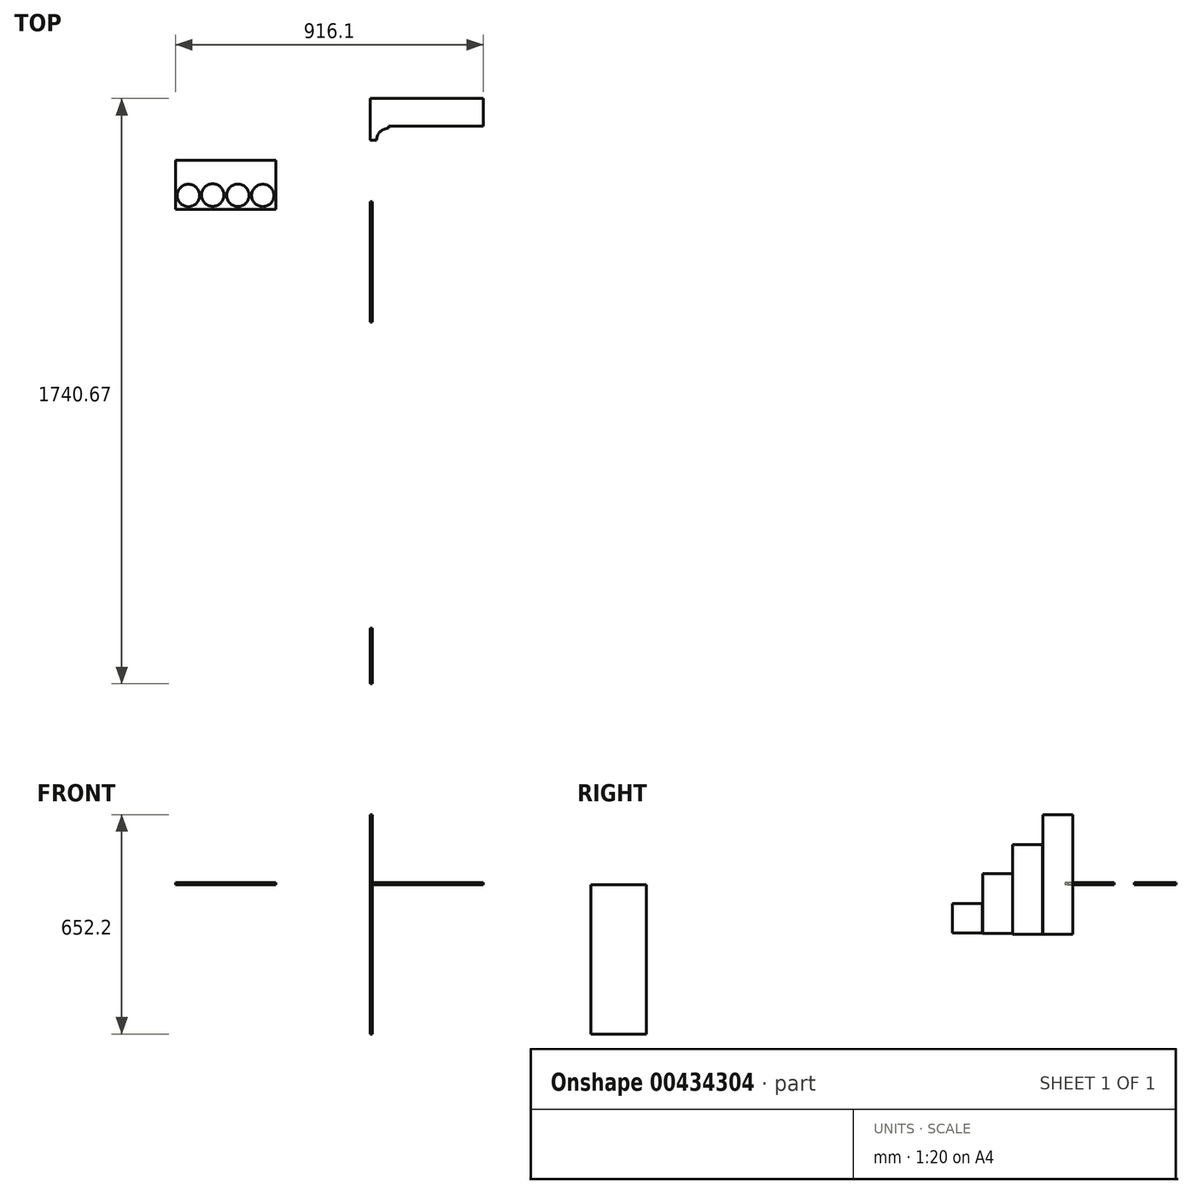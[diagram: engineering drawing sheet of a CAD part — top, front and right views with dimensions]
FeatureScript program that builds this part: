
annotation { "Feature Type Name" : "Feature", "Feature Type Description" : "" }
export const myFeature = defineFeature(function(context is Context, id is Id, definition is map)
    precondition{}
    {
        {
            var Q0;
            Q0=qCreatedBy(makeId("Top.planeOp"),FACE);
            var sketch = newSketch(context, id + "F0", { "sketchPlane" : qUnion([Q0])});
            skLineSegment(sketch, "E0.bottom", {"start": v(0, 0) * mm, "end": v(336.55, 0) * mm});
            skLineSegment(sketch, "E0.top", {"start": v(0, -165.1) * mm, "end": v(336.55, -165.1) * mm});
            skLineSegment(sketch, "E0.left", {"start": v(0, 0) * mm, "end": v(0, -165.1) * mm});
            skLineSegment(sketch, "E0.right", {"start": v(336.55, 0) * mm, "end": v(336.55, -165.1) * mm});
            skLineSegment(sketch, "E1.bottom", {"start": v(0, -82.55) * mm, "end": v(336.55, -82.55) * mm});
            skLineSegment(sketch, "E1.left", {"start": v(0, -82.55) * mm, "end": v(0, -165.1) * mm});
            skLineSegment(sketch, "E1.right", {"start": v(336.55, -82.55) * mm, "end": v(336.55, -165.1) * mm});
            skLineSegment(sketch, "E2.bottom", {"start": v(0, -82.55) * mm, "end": v(53.98, -82.55) * mm});
            skLineSegment(sketch, "E2.top", {"start": v(0, -123.83) * mm, "end": v(53.98, -123.83) * mm});
            skLineSegment(sketch, "E2.left", {"start": v(0, -82.55) * mm, "end": v(0, -123.83) * mm});
            skLineSegment(sketch, "E2.right", {"start": v(53.98, -82.55) * mm, "end": v(53.98, -123.83) * mm});
            skLineSegment(sketch, "E3.bottom", {"start": v(53.98, -82.55) * mm, "end": v(130.17, -82.55) * mm});
            skLineSegment(sketch, "E3.top", {"start": v(53.98, -123.83) * mm, "end": v(130.17, -123.83) * mm});
            skLineSegment(sketch, "E3.right", {"start": v(130.17, -82.55) * mm, "end": v(130.17, -123.83) * mm});
            skLineSegment(sketch, "E4.bottom", {"start": v(130.17, -82.55) * mm, "end": v(206.37, -82.55) * mm});
            skLineSegment(sketch, "E4.top", {"start": v(130.17, -124.58) * mm, "end": v(206.37, -124.58) * mm});
            skLineSegment(sketch, "E4.left", {"start": v(130.17, -82.55) * mm, "end": v(130.17, -124.58) * mm});
            skLineSegment(sketch, "E4.right", {"start": v(206.37, -82.55) * mm, "end": v(206.37, -124.58) * mm});
            skLineSegment(sketch, "E5.bottom", {"start": v(206.37, -82.55) * mm, "end": v(282.57, -82.55) * mm});
            skLineSegment(sketch, "E5.top", {"start": v(206.37, -124.58) * mm, "end": v(282.57, -124.58) * mm});
            skLineSegment(sketch, "E5.right", {"start": v(282.57, -82.55) * mm, "end": v(282.57, -124.58) * mm});
            skCircle(sketch, "E6", {"center": v(53.98, -123.83) * mm, "radius": 34.93 * mm});
            skCircle(sketch, "E7", {"center": v(130.17, -123.83) * mm, "radius": 34.93 * mm});
            skCircle(sketch, "E8", {"center": v(206.37, -124.58) * mm, "radius": 34.93 * mm});
            skCircle(sketch, "E9", {"center": v(282.57, -124.58) * mm, "radius": 34.93 * mm});
            skSolve(sketch);
        }
        {
            var Q0;
            Q0=makeQuery(id+"F0.imprint","IMPRINT",FACE,{"disambiguationData":[TD([[makeQuery(id+"F0.imprint","IMPRINT",EDGE,{"derivedFrom":sQuery(id+"F0.wireOp",EDGE,"E0.bottom")}),-1.0]])]});
            var Q1;
            {var subQ1=sQuery(id+"F0.wireOp",EDGE,"E2.bottom");Q1=makeQuery(id+"F0.imprint","IMPRINT",FACE,{"disambiguationData":[TD([[makeQuery(id+"F0.imprint","IMPRINT",EDGE,{"derivedFrom":subQ1}),-1.0]])]});}
            var Q2;
            {var subQ1=sQuery(id+"F0.wireOp",EDGE,"E3.bottom");Q2=makeQuery(id+"F0.imprint","IMPRINT",FACE,{"disambiguationData":[TD([[makeQuery(id+"F0.imprint","IMPRINT",EDGE,{"derivedFrom":subQ1}),-1.0]])]});}
            var Q3;
            {var subQ1=sQuery(id+"F0.wireOp",EDGE,"E4.bottom");Q3=makeQuery(id+"F0.imprint","IMPRINT",FACE,{"disambiguationData":[TD([[makeQuery(id+"F0.imprint","IMPRINT",EDGE,{"derivedFrom":subQ1}),-1.0]])]});}
            var Q4;
            {var subQ1=sQuery(id+"F0.wireOp",EDGE,"E5.bottom");Q4=makeQuery(id+"F0.imprint","IMPRINT",FACE,{"disambiguationData":[TD([[makeQuery(id+"F0.imprint","IMPRINT",EDGE,{"derivedFrom":subQ1}),-1.0]])]});}
            var Q5;
            {var subQ10=sQuery(id+"F0.wireOp",EDGE,"E1.bottom");Q5=makeQuery(id+"F0.imprint","IMPRINT",FACE,{"disambiguationData":[TD([[makeQuery(id+"F0.imprint","IMPRINT",EDGE,{"derivedFrom":subQ10}),-1.0]])]});}
            extrude(context, id + "F1", {"entities" : qUnion([Q0, Q1, Q2, Q3, Q4, Q5]), "depth" : 6.35 * mm});
        }
        {
            var Q0;
            Q0=qCreatedBy(makeId("Right.planeOp"),FACE);
            var sketch = newSketch(context, id + "F2", { "sketchPlane" : qUnion([Q0])});
            skLineSegment(sketch, "E10.bottom", {"start": v(-307.3, -147.9) * mm, "end": v(-396.2, -147.9) * mm});
            skLineSegment(sketch, "E10.top", {"start": v(-307.3, 207.7) * mm, "end": v(-396.2, 207.7) * mm});
            skLineSegment(sketch, "E10.left", {"start": v(-307.3, -147.9) * mm, "end": v(-307.3, 207.7) * mm});
            skLineSegment(sketch, "E10.right", {"start": v(-396.2, -147.9) * mm, "end": v(-396.2, 207.7) * mm});
            skSolve(sketch);
        }
        {
            var Q0;
            Q0=qCreatedBy(makeId("Right.planeOp"),FACE);
            var sketch = newSketch(context, id + "F3", { "sketchPlane" : qUnion([Q0])});
            skLineSegment(sketch, "E11.bottom", {"start": v(-396.58, -147.47) * mm, "end": v(-485.96, -147.47) * mm});
            skLineSegment(sketch, "E11.top", {"start": v(-396.58, 119.23) * mm, "end": v(-485.96, 119.23) * mm});
            skLineSegment(sketch, "E11.left", {"start": v(-396.58, -147.47) * mm, "end": v(-396.58, 119.23) * mm});
            skLineSegment(sketch, "E11.right", {"start": v(-485.96, -147.47) * mm, "end": v(-485.96, 119.23) * mm});
            skSolve(sketch);
        }
        {
            var Q0;
            Q0=qCreatedBy(makeId("Right.planeOp"),FACE);
            var sketch = newSketch(context, id + "F4", { "sketchPlane" : qUnion([Q0])});
            skLineSegment(sketch, "E12.bottom", {"start": v(-486.33, -145.61) * mm, "end": v(-575.23, -145.61) * mm});
            skLineSegment(sketch, "E12.top", {"start": v(-486.33, 32.19) * mm, "end": v(-575.23, 32.19) * mm});
            skLineSegment(sketch, "E12.left", {"start": v(-486.33, -145.61) * mm, "end": v(-486.33, 32.19) * mm});
            skLineSegment(sketch, "E12.right", {"start": v(-575.23, -145.61) * mm, "end": v(-575.23, 32.19) * mm});
            skSolve(sketch);
        }
        {
            var Q0;
            Q0=qCreatedBy(makeId("Right.planeOp"),FACE);
            var sketch = newSketch(context, id + "F5", { "sketchPlane" : qUnion([Q0])});
            skLineSegment(sketch, "E13.bottom", {"start": v(-575.85, -144.48) * mm, "end": v(-664.75, -144.48) * mm});
            skLineSegment(sketch, "E13.top", {"start": v(-575.85, -56.2) * mm, "end": v(-664.75, -56.2) * mm});
            skLineSegment(sketch, "E13.left", {"start": v(-575.85, -144.48) * mm, "end": v(-575.85, -56.2) * mm});
            skLineSegment(sketch, "E13.right", {"start": v(-664.75, -144.48) * mm, "end": v(-664.75, -56.2) * mm});
            skSolve(sketch);
        }
        {
            var Q0;
            Q0=qCreatedBy(makeId("Right.planeOp"),FACE);
            var sketch = newSketch(context, id + "F6", { "sketchPlane" : qUnion([Q0])});
            skLineSegment(sketch, "E14.bottom", {"start": v(-1740.67, -444.5) * mm, "end": v(-1575.57, -444.5) * mm});
            skLineSegment(sketch, "E14.top", {"start": v(-1740.67, 0) * mm, "end": v(-1575.57, 0) * mm});
            skLineSegment(sketch, "E14.left", {"start": v(-1740.67, -444.5) * mm, "end": v(-1740.67, 0) * mm});
            skLineSegment(sketch, "E14.right", {"start": v(-1575.57, -444.5) * mm, "end": v(-1575.57, 0) * mm});
            skSolve(sketch);
        }
        {
            var Q0;
            Q0=makeQuery(id+"F6.imprint","IMPRINT",FACE,{"disambiguationData":[TD([[makeQuery(id+"F6.imprint","IMPRINT",EDGE,{"derivedFrom":sQuery(id+"F6.wireOp",EDGE,"E14.bottom")}),1.0]])]});
            var Q1;
            Q1=makeQuery(id+"F5.imprint","IMPRINT",FACE,{"disambiguationData":[TD([[makeQuery(id+"F5.imprint","IMPRINT",EDGE,{"derivedFrom":sQuery(id+"F5.wireOp",EDGE,"E13.bottom")}),-1.0]])]});
            var Q2;
            Q2=makeQuery(id+"F4.imprint","IMPRINT",FACE,{"disambiguationData":[TD([[makeQuery(id+"F4.imprint","IMPRINT",EDGE,{"derivedFrom":sQuery(id+"F4.wireOp",EDGE,"E12.bottom")}),-1.0]])]});
            var Q3;
            Q3=makeQuery(id+"F3.imprint","IMPRINT",FACE,{"disambiguationData":[TD([[makeQuery(id+"F3.imprint","IMPRINT",EDGE,{"derivedFrom":sQuery(id+"F3.wireOp",EDGE,"E11.bottom")}),-1.0]])]});
            var Q4;
            Q4=makeQuery(id+"F2.imprint","IMPRINT",FACE,{"disambiguationData":[TD([[makeQuery(id+"F2.imprint","IMPRINT",EDGE,{"derivedFrom":sQuery(id+"F2.wireOp",EDGE,"E10.bottom")}),-1.0]])]});
            extrude(context, id + "F7", {"entities" : qUnion([Q0, Q1, Q2, Q3, Q4]), "depth" : 6.35 * mm});
        }
        {
            var Q0;
            Q0=qCreatedBy(makeId("Top.planeOp"),FACE);
            var sketch = newSketch(context, id + "F8", { "sketchPlane" : qUnion([Q0])});
            skLineSegment(sketch, "E15.bottom", {"start": v(-579.55, -183.6) * mm, "end": v(-281.1, -183.6) * mm});
            skLineSegment(sketch, "E15.top", {"start": v(-579.55, -329.65) * mm, "end": v(-281.1, -329.65) * mm});
            skLineSegment(sketch, "E15.left", {"start": v(-579.55, -183.6) * mm, "end": v(-579.55, -329.65) * mm});
            skLineSegment(sketch, "E15.right", {"start": v(-281.1, -183.6) * mm, "end": v(-281.1, -329.65) * mm});
            skSolve(sketch);
        }
        {
            var Q0;
            Q0=makeQuery(id+"F8.imprint","IMPRINT",FACE,{"disambiguationData":[TD([[makeQuery(id+"F8.imprint","IMPRINT",EDGE,{"derivedFrom":sQuery(id+"F8.wireOp",EDGE,"E15.bottom")}),-1.0]])]});
            var sketch = newSketch(context, id + "F9", { "sketchPlane" : qUnion([Q0])});
            skLineSegment(sketch, "E16", {"start": v(-540.86, -327.6) * mm, "end": v(-540.86, -288.35) * mm});
            skLineSegment(sketch, "E17", {"start": v(-468.67, -327.41) * mm, "end": v(-468.67, -287.15) * mm});
            skLineSegment(sketch, "E18", {"start": v(-393.69, -327.93) * mm, "end": v(-393.69, -288.06) * mm});
            skLineSegment(sketch, "E19", {"start": v(-319.64, -327.93) * mm, "end": v(-319.64, -288.24) * mm});
            skSolve(sketch);
        }
        {
            var Q0;
            Q0=makeQuery(id+"F8.imprint","IMPRINT",FACE,{"disambiguationData":[TD([[makeQuery(id+"F8.imprint","IMPRINT",EDGE,{"derivedFrom":sQuery(id+"F8.wireOp",EDGE,"E15.bottom")}),-1.0]])]});
            extrude(context, id + "F10", {"entities" : qUnion([Q0]), "depth" : 6.35 * mm});
        }
        {
            var Q0;
            Q0=sQuery(id+"F9.wireOp",VERTEX,"E16.end");
            var Q1;
            Q1=sQuery(id+"F9.wireOp",VERTEX,"E17.end");
            var Q2;
            Q2=sQuery(id+"F9.wireOp",VERTEX,"E18.end");
            var Q3;
            Q3=sQuery(id+"F9.wireOp",VERTEX,"E19.end");
            var Q4;
            Q4=makeQuery(id+"F10.opExtrude","SWEPT_BODY",BODY,{"disambiguationData":[OSD([sQuery(id+"F8.wireOp",EDGE,"E15.bottom"),sQuery(id+"F8.wireOp",EDGE,"E15.top"),sQuery(id+"F8.wireOp",EDGE,"E15.left"),sQuery(id+"F8.wireOp",EDGE,"E15.right")])]});
            hole(context, id + "F11", {"style" : HoleStyle.SIMPLE, "endStyle" : HoleEndStyle.BLIND, "oppositeDirection" : true, "holeDiameter" : 66.67 * mm, "holeDepth" : 12.7 * mm, "isTappedThrough" : true, "tappedDepth" : 12.7 * mm, "tapClearance" : 3, "locations" : qUnion([Q0, Q1, Q2, Q3]), "scope" : qUnion([Q4])});
        }
    });
